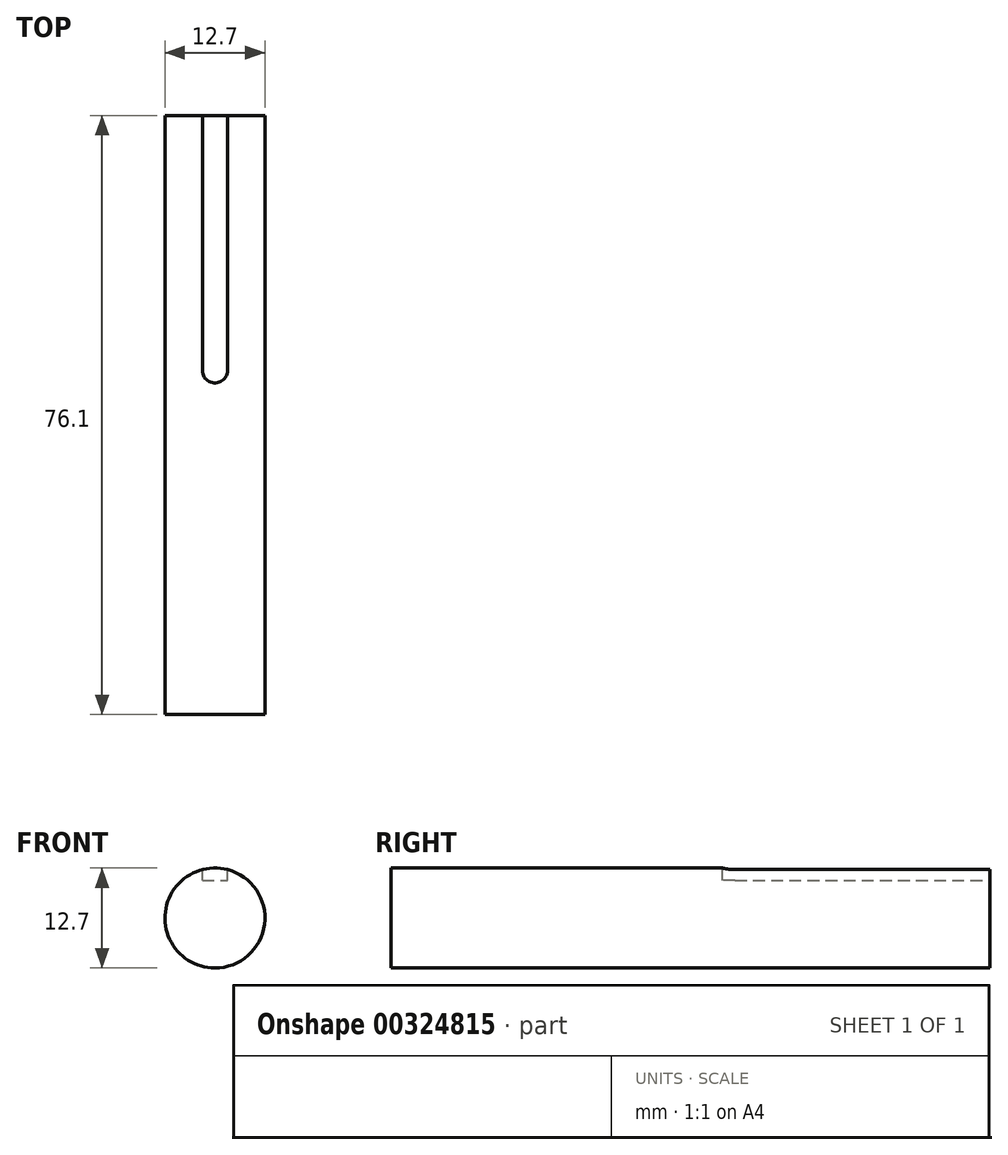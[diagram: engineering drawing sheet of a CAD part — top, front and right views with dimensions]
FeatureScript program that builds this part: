
annotation { "Feature Type Name" : "Feature", "Feature Type Description" : "" }
export const myFeature = defineFeature(function(context is Context, id is Id, definition is map)
    precondition{}
    {
        {
            var Q0;
            Q0=qCreatedBy(makeId("Front.planeOp"),FACE);
            var sketch = newSketch(context, id + "F0", { "sketchPlane" : qUnion([Q0])});
            skCircle(sketch, "E0", {"center": v(0, 0) * mm, "radius": 6.35 * mm});
            skSolve(sketch);
        }
        {
            var Q0;
            Q0=makeQuery(id+"F0.imprint","IMPRINT",FACE,{"disambiguationData":[TD([[makeQuery(id+"F0.imprint","IMPRINT",EDGE,{"derivedFrom":sQuery(id+"F0.wireOp",EDGE,"E0")}),1.0]])]});
            extrude(context, id + "F1", {"entities" : qUnion([Q0]), "depth" : 76.1 * mm, "offsetDistance" : 25.4 * mm});
        }
        {
            var Q0;
            Q0=qCreatedBy(makeId("Top.planeOp"),FACE);
            cPlane(context, id + "F2", {"entities" : qUnion([Q0]), "cplaneType" : CPlaneType.OFFSET, "offset" : 6.35 * mm, "width" : 152.4 * mm, "height" : 152.4 * mm});
        }
        {
            var Q0;
            Q0=qCreatedBy(id+"F2.planeOp",FACE);
            var sketch = newSketch(context, id + "F3", { "sketchPlane" : qUnion([Q0])});
            skArc(sketch, "E1", {"start": v(-1.59, -32.39) * mm, "mid": v(0, -33.97) * mm, "end": v(1.59, -32.39) * mm});
            skLineSegment(sketch, "E2", {"start": v(-1.59, -32.39) * mm, "end": v(-1.59, 0) * mm});
            skLineSegment(sketch, "E3.MirrorCS", {"start": v(1.59, -32.39) * mm, "end": v(1.59, 0) * mm});
            skLineSegment(sketch, "E4", {"start": v(-1.59, 0) * mm, "end": v(1.59, 0) * mm});
            skSolve(sketch);
        }
        {
            var Q0;
            Q0=makeQuery(id+"F3.imprint","IMPRINT",FACE,{"disambiguationData":[TD([[makeQuery(id+"F3.imprint","IMPRINT",EDGE,{"derivedFrom":sQuery(id+"F3.wireOp",EDGE,"E1")}),1.0]])]});
            extrude(context, id + "F4", {"entities" : qUnion([Q0]), "operationType" : NewBodyOperationType.REMOVE, "oppositeDirection" : true, "depth" : 1.6 * mm, "offsetDistance" : 25.4 * mm});
        }
    });
